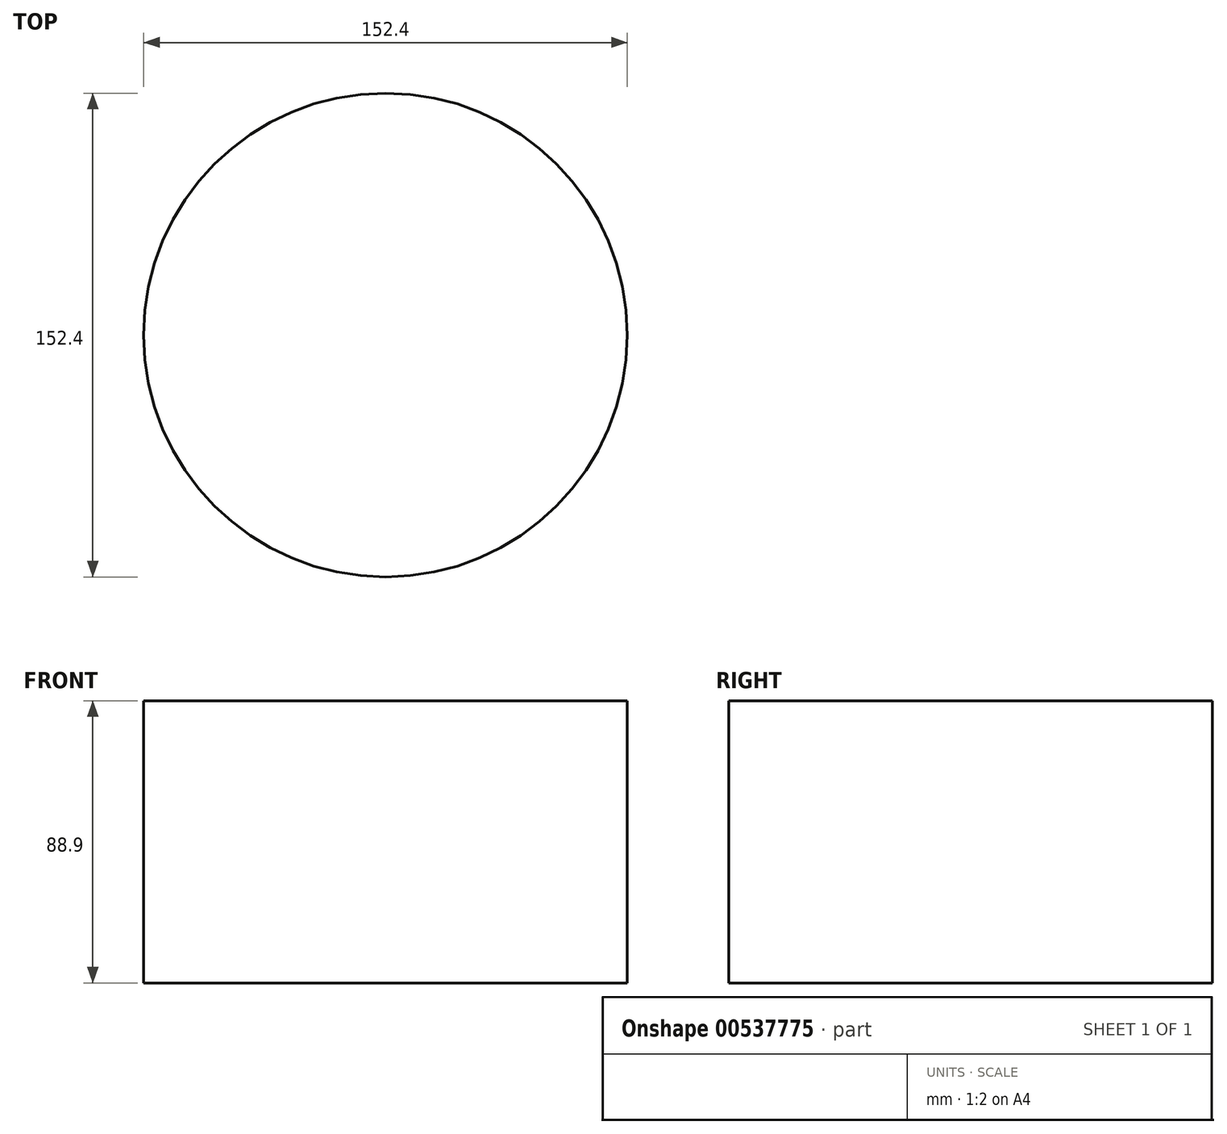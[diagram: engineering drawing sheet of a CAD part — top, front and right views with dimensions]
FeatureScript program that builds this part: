
annotation { "Feature Type Name" : "Feature", "Feature Type Description" : "" }
export const myFeature = defineFeature(function(context is Context, id is Id, definition is map)
    precondition{}
    {
        {
            var Q0;
            Q0=qCreatedBy(makeId("Top.planeOp"),FACE);
            var sketch = newSketch(context, id + "F0", { "sketchPlane" : qUnion([Q0])});
            skCircle(sketch, "E0", {"center": v(0, 0) * mm, "radius": 76.2 * mm});
            skSolve(sketch);
        }
        {
            var Q0;
            Q0 = qSketchRegion(id + "F0", true);
            extrude(context, id + "F1", {"entities" : qUnion([Q0]), "endBound" : BoundingType.SYMMETRIC, "depth" : 88.9 * mm, "offsetDistance" : 25.4 * mm});
        }
    });
